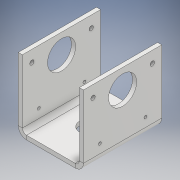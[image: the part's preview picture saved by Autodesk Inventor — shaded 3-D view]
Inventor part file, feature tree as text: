
AUTODESK INVENTOR PART (.ipt)
format: ipt  version: 2018 (Build 220112000, 112)  size: 179,200 bytes
history: native  units: mm
features: sketch x6, sheet_metal_op x4, other x4, hole x2, projected_geometry x2
ambient origin geometry x8: Origin, YZ Plane, XZ Plane, XY Plane, X Axis, Y Axis, Z Axis, Center Point
bodies: Solid1 (feature_tree)
feature tree (18):
  sheet_metal_op  "Face1"
  sheet_metal_op  "Flange1"
  hole  "Hole1"  [1 undecoded]
  hole  "Hole2"  [1 undecoded]
  sketch  "Sketch1"  dims[d0=100.0mm d1=120.0mm]
  other  "Plate1"
  sketch  "Sketch2"  dims[d2=6.35mm d3=6.35mm]
  other  "Plate2"
  sheet_metal_op  "Bend1"
  sheet_metal_op  "Corner1"
  sketch  "Sketch3"  dims[d4=3.175mm]
  sketch  "Sketch4"  dims[d5=12.7mm]
  sketch  "Sketch5"  dims[d6=6.35mm]
  projected_geometry  "Projected Loop1"
  sketch  "Sketch6"  dims[d7=110.0mm d8=90.0deg d9=6.35mm d10=25.4mm d11=6.35mm d12=6.35mm d13=42.164mm d14=43.0mm d15=80.0mm d16=6.35mm d17=0.0mm d18=31.0mm d19=6.35mm d20=0.0mm d22=6.6mm d23=6.0mm d24=12.6mm d25=2.0mm d26=90.0deg d27=6.35mm d28=20.594885mm d29=70.0mm d30=83.542mm d31=4.5mm d32=6.0mm d33=9.4mm d34=2.0mm d35=90.0deg d36=6.35mm d37=20.594885mm d38=17.542mm d39=45.5mm]
  projected_geometry  "Projected Loop2"
  other  "Cut1"
  other  "Cut2"
note: 2 required parameter values undecoded (feature->parameter linkage not recoverable at this tier; creation-order binding heuristic only, values carry confidence <= 0.55)
